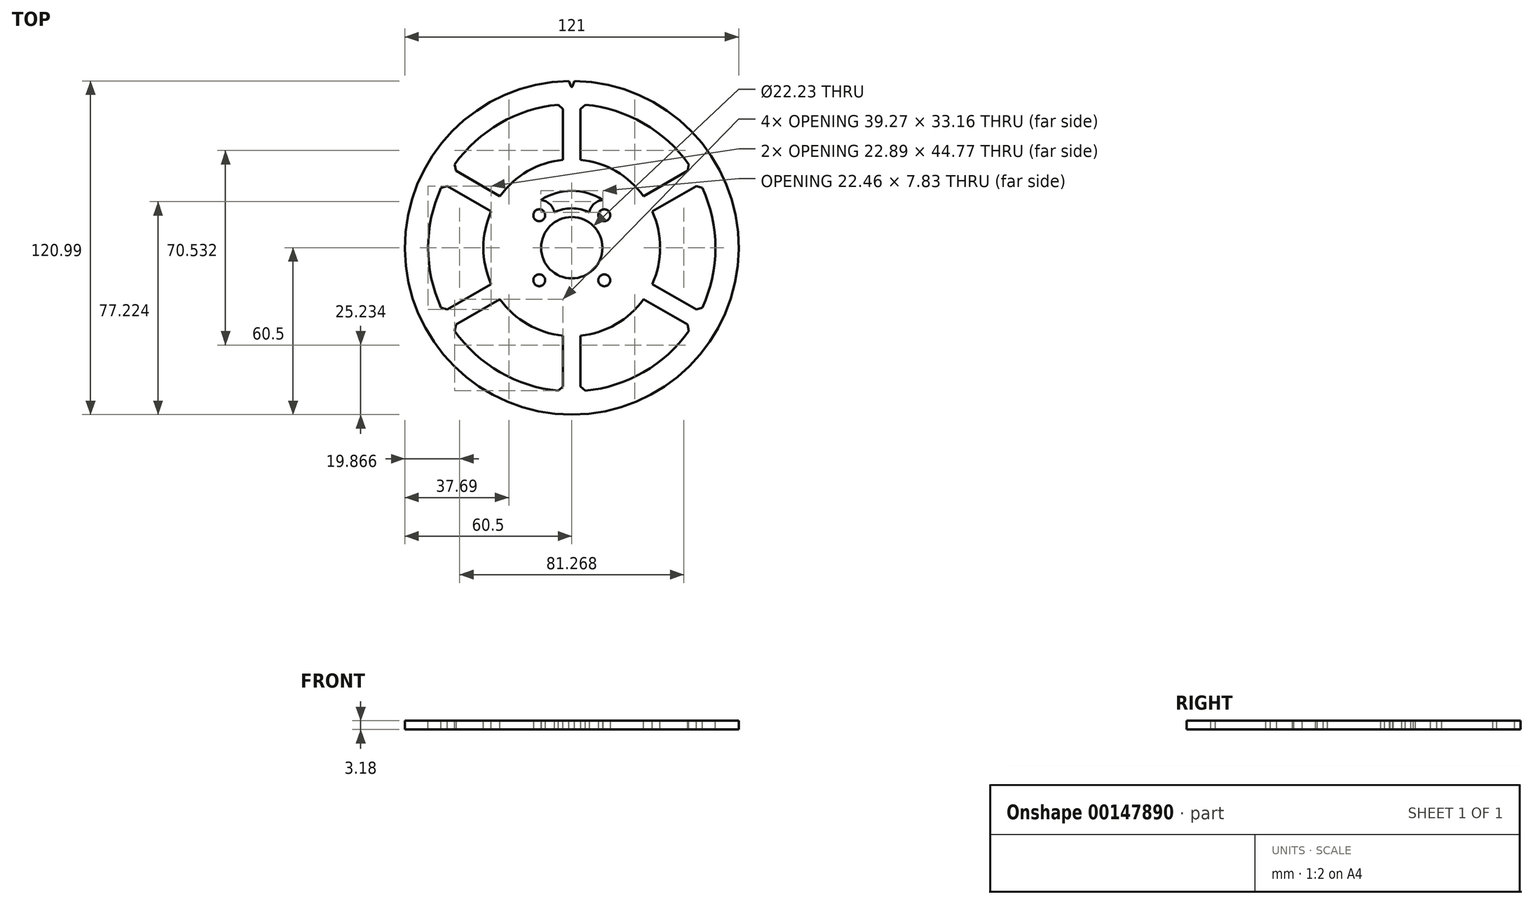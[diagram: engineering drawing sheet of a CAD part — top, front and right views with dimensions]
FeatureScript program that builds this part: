
annotation { "Feature Type Name" : "Feature", "Feature Type Description" : "" }
export const myFeature = defineFeature(function(context is Context, id is Id, definition is map)
    precondition{}
    {
        {
            var Q0;
            Q0=qCreatedBy(makeId("Top.planeOp"),FACE);
            var sketch = newSketch(context, id + "F0", { "sketchPlane" : qUnion([Q0])});
            skCircle(sketch, "E0", {"center": v(0, 0) * mm, "radius": 60.5 * mm});
            skCircle(sketch, "E1", {"center": v(0, 0) * mm, "radius": 11.11 * mm});
            skLineSegment(sketch, "E2.bottom", {"start": v(-11.79, -11.79) * mm, "end": v(11.79, -11.79) * mm, "construction": true});
            skLineSegment(sketch, "E2.top", {"start": v(-11.79, 11.79) * mm, "end": v(11.79, 11.79) * mm, "construction": true});
            skLineSegment(sketch, "E2.left", {"start": v(-11.79, -11.79) * mm, "end": v(-11.79, 11.79) * mm, "construction": true});
            skLineSegment(sketch, "E2.right", {"start": v(11.79, -11.79) * mm, "end": v(11.79, 11.79) * mm, "construction": true});
            skCircle(sketch, "E3", {"center": v(-11.79, -11.79) * mm, "radius": 5.56 * mm, "construction": true});
            skCircle(sketch, "E4", {"center": v(-11.79, -11.79) * mm, "radius": 2.15 * mm});
            skCircle(sketch, "E5", {"center": v(11.79, 11.79) * mm, "radius": 2.15 * mm});
            skCircle(sketch, "E6", {"center": v(11.79, -11.79) * mm, "radius": 2.15 * mm});
            skCircle(sketch, "E7", {"center": v(-11.79, 11.79) * mm, "radius": 2.15 * mm});
            skSolve(sketch);
        }
        {
            var Q0;
            Q0=makeQuery(id+"F0.imprint","IMPRINT",FACE,{"disambiguationData":[TD([[makeQuery(id+"F0.imprint","IMPRINT",EDGE,{"derivedFrom":sQuery(id+"F0.wireOp",EDGE,"d7zeTPih-CRss-xDOh-gPdP-rmPCdwzH7cdN.left")}),1.0]])]});
            var Q1;
            Q1=makeQuery(id+"F0.imprint","IMPRINT",FACE,{"disambiguationData":[TD([[makeQuery(id+"F0.imprint","IMPRINT",EDGE,{"derivedFrom":sQuery(id+"F0.wireOp",EDGE,"E0")}),1.0]])]});
            extrude(context, id + "F1", {"entities" : qUnion([Q0, Q1]), "depth" : 3.17 * mm});
        }
        {
            var Q0;
            Q0=makeQuery(id+"F1.opExtrude","CAP_FACE",FACE,{"disambiguationData":[OSD([sQuery(id+"F0.wireOp",EDGE,"d7zeTPih-CRss-xDOh-gPdP-rmPCdwzH7cdN.left"),sQuery(id+"F0.wireOp",EDGE,"d7zeTPih-CRss-xDOh-gPdP-rmPCdwzH7cdN.right"),sQuery(id+"F0.wireOp",EDGE,"ScfBMfkV-s1yN-Ls9R-SGr5-fEyGpD6zak8e"),sQuery(id+"F0.wireOp",EDGE,"xnxmVwjl-FvSF-m7sj-be2U-u85gZZGoORGZ"),sQuery(id+"F0.wireOp",EDGE,"E0")])],"isStart":false});
            var sketch = newSketch(context, id + "F2", { "sketchPlane" : qUnion([Q0])});
            skLineSegment(sketch, "E8", {"start": v(0, 0) * mm, "end": v(0, 60.5) * mm, "construction": true});
            skLineSegment(sketch, "E9", {"start": v(0, 0) * mm, "end": v(0.66, 60.5) * mm, "construction": true});
            skArc(sketch, "E10", {"start": v(1.02, 60.5) * mm, "mid": v(0, 60.5) * mm, "end": v(-1.02, 60.5) * mm});
            skLineSegment(sketch, "E11", {"start": v(-1.02, 60.5) * mm, "end": v(-0.28, 58.52) * mm});
            skLineSegment(sketch, "E12", {"start": v(1.02, 60.5) * mm, "end": v(0.28, 58.52) * mm});
            skPoint(sketch, "E13", {"position": v(0.65, 59.5) * mm});
            skArc(sketch, "E14", {"start": v(-0.28, 58.52) * mm, "mid": v(0, 58.33) * mm, "end": v(0.28, 58.52) * mm});
            skSolve(sketch);
        }
        {
            var Q0;
            Q0=qSketchRegion(id+"F2",true);
            var Q1;
            Q1=makeQuery(id+"F1.opExtrude","CAP_FACE",FACE,{"disambiguationData":[OSD([sQuery(id+"F0.wireOp",EDGE,"d7zeTPih-CRss-xDOh-gPdP-rmPCdwzH7cdN.left"),sQuery(id+"F0.wireOp",EDGE,"d7zeTPih-CRss-xDOh-gPdP-rmPCdwzH7cdN.right"),sQuery(id+"F0.wireOp",EDGE,"ScfBMfkV-s1yN-Ls9R-SGr5-fEyGpD6zak8e"),sQuery(id+"F0.wireOp",EDGE,"xnxmVwjl-FvSF-m7sj-be2U-u85gZZGoORGZ"),sQuery(id+"F0.wireOp",EDGE,"E0")])],"isStart":true});
            extrude(context, id + "F3", {"entities" : qUnion([Q0]), "operationType" : NewBodyOperationType.REMOVE, "endBound" : BoundingType.UP_TO_SURFACE, "oppositeDirection" : true, "endBoundEntityFace" : qUnion([Q1]), "depth" : 25.4 * mm});
        }
        {
            var Q0;
            Q0=makeQuery(id+"F1.opExtrude","CAP_FACE",FACE,{"disambiguationData":[OSD([sQuery(id+"F0.wireOp",EDGE,"E0"),sQuery(id+"F0.wireOp",EDGE,"E1"),sQuery(id+"F0.wireOp",EDGE,"E4"),sQuery(id+"F0.wireOp",EDGE,"E5"),sQuery(id+"F0.wireOp",EDGE,"E6"),sQuery(id+"F0.wireOp",EDGE,"E7")])],"isStart":false});
            var sketch = newSketch(context, id + "F4", { "sketchPlane" : qUnion([Q0])});
            skLineSegment(sketch, "E15", {"start": v(0, 0) * mm, "end": v(0, 31.87) * mm, "construction": true});
            skLineSegment(sketch, "E16", {"start": v(0, 31.87) * mm, "end": v(3.18, 31.87) * mm, "construction": true});
            skLineSegment(sketch, "E17", {"start": v(3.17, 51.98) * mm, "end": v(0, 51.98) * mm, "construction": true});
            skLineSegment(sketch, "E18", {"start": v(0, 51.98) * mm, "end": v(0, 58.33) * mm, "construction": true});
            skLineSegment(sketch, "E19", {"start": v(0, 0) * mm, "end": v(27.6, 15.94) * mm, "construction": true});
            skCircle(sketch, "E20", {"center": v(0, 0) * mm, "radius": 58.33 * mm, "construction": true});
            skLineSegment(sketch, "E21", {"start": v(27.6, 15.94) * mm, "end": v(26.01, 18.69) * mm, "construction": true});
            skArc(sketch, "E22", {"start": v(26.01, 18.69) * mm, "mid": v(16.01, 27.74) * mm, "end": v(3.18, 31.87) * mm});
            skLineSegment(sketch, "E23", {"start": v(3.18, 31.87) * mm, "end": v(3.18, 51.98) * mm});
            skLineSegment(sketch, "E24", {"start": v(26.01, 18.69) * mm, "end": v(43.43, 28.74) * mm});
            skArc(sketch, "E25", {"start": v(43.43, 28.74) * mm, "mid": v(26.04, 45.1) * mm, "end": v(3.18, 51.98) * mm});
            skSolve(sketch);
        }
        {
            var Q0;
            Q0=qSketchRegion(id+"F4",true);
            var Q1;
            Q1=makeQuery(id+"F1.opExtrude","CAP_FACE",FACE,{"disambiguationData":[OSD([sQuery(id+"F0.wireOp",EDGE,"E0"),sQuery(id+"F0.wireOp",EDGE,"E1"),sQuery(id+"F0.wireOp",EDGE,"E4"),sQuery(id+"F0.wireOp",EDGE,"E5"),sQuery(id+"F0.wireOp",EDGE,"E6"),sQuery(id+"F0.wireOp",EDGE,"E7")])],"isStart":true});
            extrude(context, id + "F5", {"entities" : qUnion([Q0]), "operationType" : NewBodyOperationType.REMOVE, "endBound" : BoundingType.UP_TO_SURFACE, "oppositeDirection" : true, "endBoundEntityFace" : qUnion([Q1]), "depth" : 25.4 * mm});
        }
        {
            var Q0;
            Q0=makeQuery(id+"F5.boolean.opBoolean","COPY",EDGE,{"derivedFrom":makeQuery(id+"F5.opExtrude","SWEPT_EDGE",EDGE,{"disambiguationData":[OSD([sQuery(id+"F4.wireOp",EDGE,"E23"),sQuery(id+"F4.wireOp",EDGE,"E25")])]})});
            var Q1;
            Q1=makeQuery(id+"F5.boolean.opBoolean","COPY",EDGE,{"derivedFrom":makeQuery(id+"F5.opExtrude","SWEPT_EDGE",EDGE,{"disambiguationData":[OSD([sQuery(id+"F4.wireOp",EDGE,"E24"),sQuery(id+"F4.wireOp",EDGE,"E25")])]})});
            chamfer(context, id + "F6", {"entities" : qUnion([Q0, Q1]), "width" : 1.59 * mm, "tangentPropagation" : true});
        }
        {
            var Q0;
            Q0=makeQuery(id+"F6.opChamfer","BLEND_FACE",FACE,{"disambiguationData":[OSD([sQuery(id+"F4.wireOp",EDGE,"E24"),sQuery(id+"F4.wireOp",EDGE,"E25")])]});
            var Q1;
            Q1=makeQuery(id+"F5.boolean.opBoolean","COPY",FACE,{"derivedFrom":makeQuery(id+"F5.opExtrude","SWEPT_FACE",FACE,{"disambiguationData":[OSD([sQuery(id+"F4.wireOp",EDGE,"E24")])]})});
            var Q2;
            Q2=makeQuery(id+"F5.boolean.opBoolean","COPY",FACE,{"derivedFrom":makeQuery(id+"F5.opExtrude","SWEPT_FACE",FACE,{"disambiguationData":[OSD([sQuery(id+"F4.wireOp",EDGE,"E25")])]})});
            var Q3;
            Q3=makeQuery(id+"F6.opChamfer","BLEND_FACE",FACE,{"disambiguationData":[OSD([sQuery(id+"F4.wireOp",EDGE,"E23"),sQuery(id+"F4.wireOp",EDGE,"E25")])]});
            var Q4;
            Q4=makeQuery(id+"F5.boolean.opBoolean","COPY",FACE,{"derivedFrom":makeQuery(id+"F5.opExtrude","SWEPT_FACE",FACE,{"disambiguationData":[OSD([sQuery(id+"F4.wireOp",EDGE,"E23")])]})});
            var Q5;
            Q5=makeQuery(id+"F5.boolean.opBoolean","COPY",FACE,{"derivedFrom":makeQuery(id+"F5.opExtrude","SWEPT_FACE",FACE,{"disambiguationData":[OSD([sQuery(id+"F4.wireOp",EDGE,"E22")])]})});
            var Q6;
            Q6=makeQuery(id+"F1.opExtrude","SWEPT_FACE",FACE,{"disambiguationData":[OSD([sQuery(id+"F0.wireOp",EDGE,"E1")])]});
            circularPattern(context, id + "F7", {"patternType" : PatternType.FACE, "faces" : qUnion([Q0, Q1, Q2, Q3, Q4, Q5]), "axis" : qUnion([Q6]), "angle" : 60 * degree, "instanceCount" : 6});
        }
        {
            var Q0;
            Q0=makeQuery(id+"F1.opExtrude","CAP_FACE",FACE,{"disambiguationData":[OSD([sQuery(id+"F0.wireOp",EDGE,"E0"),sQuery(id+"F0.wireOp",EDGE,"E1"),sQuery(id+"F0.wireOp",EDGE,"E4"),sQuery(id+"F0.wireOp",EDGE,"E5"),sQuery(id+"F0.wireOp",EDGE,"E6"),sQuery(id+"F0.wireOp",EDGE,"E7")])],"isStart":true});
            var sketch = newSketch(context, id + "F8", { "sketchPlane" : qUnion([Q0])});
            skArc(sketch, "E26", {"start": v(6.33, -12.81) * mm, "mid": v(8.03, -15.88) * mm, "end": v(11.23, -17.31) * mm});
            skArc(sketch, "E27", {"start": v(-11.23, -17.31) * mm, "mid": v(-8.03, -15.88) * mm, "end": v(-6.33, -12.81) * mm});
            skArc(sketch, "E28", {"start": v(-6.33, -12.81) * mm, "mid": v(0, -14.29) * mm, "end": v(6.33, -12.81) * mm});
            skArc(sketch, "E29", {"start": v(-11.23, -17.31) * mm, "mid": v(0, -20.64) * mm, "end": v(11.23, -17.31) * mm});
            skSolve(sketch);
        }
        {
            var Q0;
            Q0=qSketchRegion(id+"F8",true);
            var Q1;
            Q1=makeQuery(id+"F1.opExtrude","CAP_FACE",FACE,{"disambiguationData":[OSD([sQuery(id+"F0.wireOp",EDGE,"E0"),sQuery(id+"F0.wireOp",EDGE,"E1"),sQuery(id+"F0.wireOp",EDGE,"E4"),sQuery(id+"F0.wireOp",EDGE,"E5"),sQuery(id+"F0.wireOp",EDGE,"E6"),sQuery(id+"F0.wireOp",EDGE,"E7")])],"isStart":false});
            extrude(context, id + "F9", {"entities" : qUnion([Q0]), "operationType" : NewBodyOperationType.REMOVE, "endBound" : BoundingType.UP_TO_SURFACE, "oppositeDirection" : true, "endBoundEntityFace" : qUnion([Q1]), "depth" : 25.4 * mm});
        }
    });
